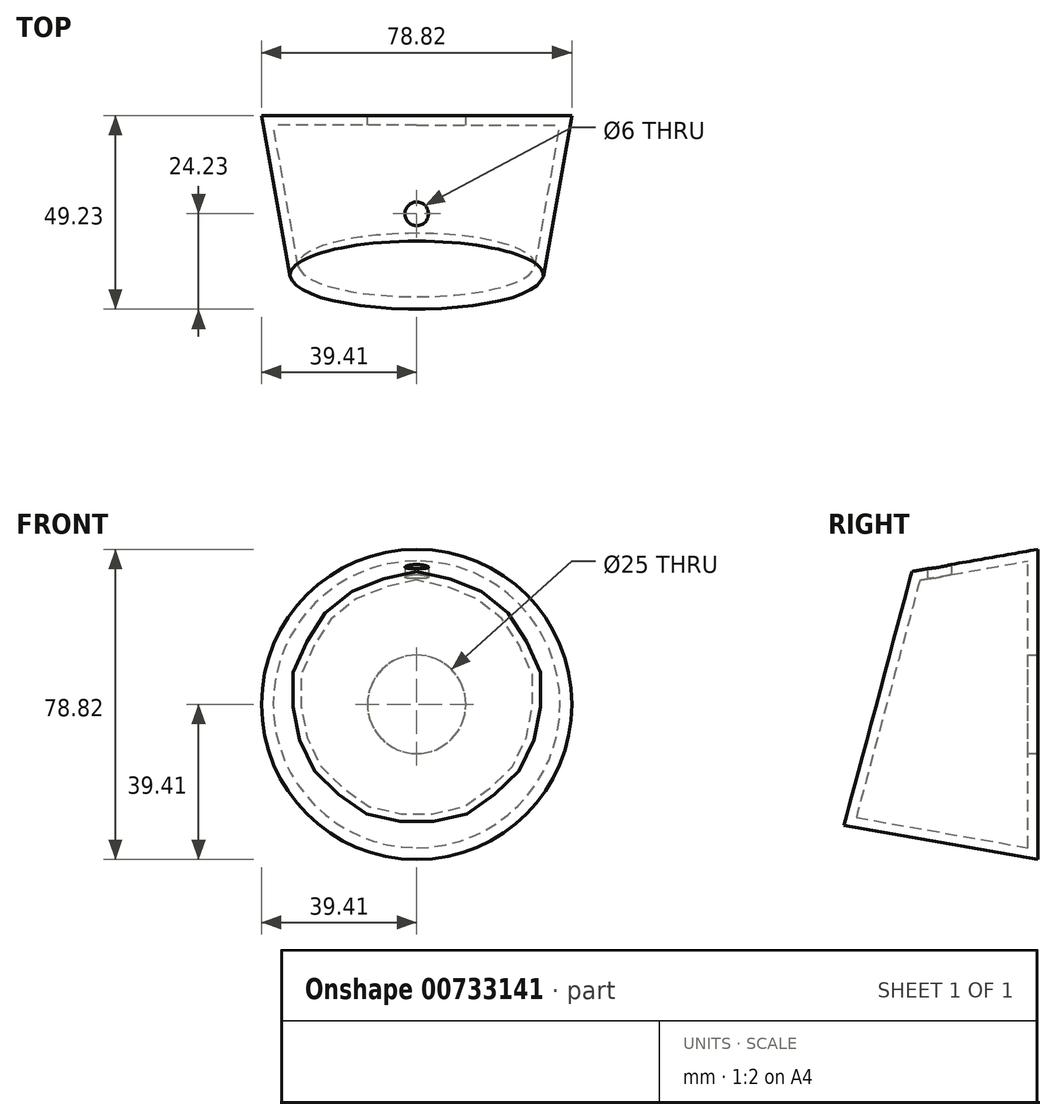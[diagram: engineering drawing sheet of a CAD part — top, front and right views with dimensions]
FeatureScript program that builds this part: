
annotation { "Feature Type Name" : "Feature", "Feature Type Description" : "" }
export const myFeature = defineFeature(function(context is Context, id is Id, definition is map)
    precondition{}
    {
        {
            var Q0;
            Q0=qCreatedBy(makeId("Front.planeOp"),FACE);
            var sketch = newSketch(context, id + "F0", { "sketchPlane" : qUnion([Q0])});
            skCircle(sketch, "E0", {"center": v(0, 0) * mm, "radius": 35 * mm});
            skSolve(sketch);
        }
        {
            var Q0;
            Q0=makeQuery(id+"F0.imprint","IMPRINT",FACE,{"disambiguationData":[TD([[makeQuery(id+"F0.imprint","IMPRINT",EDGE,{"derivedFrom":sQuery(id+"F0.wireOp",EDGE,"E0")}),1.0]])]});
            var Q1;
            Q1=sQuery(id+"F0.wireOp",EDGE,"E0");
            extrude(context, id + "F1", {"entities" : qUnion([Q0]), "surfaceEntities" : qUnion([Q1]), "oppositeDirection" : true, "depth" : 25 * mm, "offsetDistance" : 25 * mm, "hasDraft" : true, "draftAngle" : 10 * degree});
        }
        {
            var Q0;
            Q0 = qSketchRegion(id + "F0", true);
            extrude(context, id + "F2", {"entities" : qUnion([Q0]), "operationType" : NewBodyOperationType.ADD, "depth" : 25 * mm, "offsetDistance" : 25 * mm, "hasDraft" : true, "draftAngle" : 10 * degree, "draftPullDirection" : true});
        }
        {
            var Q0;
            Q0=qCreatedBy(makeId("Right.planeOp"),FACE);
            var sketch = newSketch(context, id + "F3", { "sketchPlane" : qUnion([Q0])});
            skLineSegment(sketch, "E1", {"start": v(-5.75, 38.26) * mm, "end": v(-29.22, -49.32) * mm});
            skLineSegment(sketch, "E2", {"start": v(-5.75, 38.26) * mm, "end": v(-37.5, 38.26) * mm});
            skLineSegment(sketch, "E3", {"start": v(-37.5, 38.26) * mm, "end": v(-37.5, -49.69) * mm});
            skLineSegment(sketch, "E4", {"start": v(-29.22, -49.32) * mm, "end": v(-37.5, -49.69) * mm});
            skLineSegment(sketch, "E5", {"start": v(-99.85, 0) * mm, "end": v(0, 0) * mm, "construction": true});
            skSolve(sketch);
        }
        {
            var Q0;
            Q0=makeQuery(id+"F3.imprint","IMPRINT",FACE,{"disambiguationData":[TD([[makeQuery(id+"F3.imprint","IMPRINT",EDGE,{"derivedFrom":sQuery(id+"F3.wireOp",EDGE,"E1")}),-1.0]])]});
            extrude(context, id + "F4", {"entities" : qUnion([Q0]), "operationType" : NewBodyOperationType.REMOVE, "endBound" : BoundingType.SYMMETRIC, "oppositeDirection" : true, "depth" : 80 * mm, "offsetDistance" : 25 * mm});
        }
        {
            var Q0;
            Q0=makeQuery(id+"F1.opExtrude","CAP_FACE",FACE,{"disambiguationData":[OSD([sQuery(id+"F0.wireOp",EDGE,"E0")])],"isStart":true});
            var Q1;
            Q1=makeQuery(id+"F1.*.split.splitOp","SPLIT",FACE,{"derivedFrom":makeQuery(id+"F1.opExtrude","SWEPT_FACE",FACE,{"disambiguationData":[OSD([sQuery(id+"F0.wireOp",EDGE,"E0")])]}),"isFromBackBody":true});
            var Q2;
            Q2=makeQuery(id+"F1.*.split.splitOp","SPLIT",FACE,{"derivedFrom":makeQuery(id+"F1.opExtrude","SWEPT_FACE",FACE,{"disambiguationData":[OSD([sQuery(id+"F0.wireOp",EDGE,"E0")])]})});
            var Q3;
            Q3=makeQuery(id+"F4.boolean.opBoolean","COPY",FACE,{"derivedFrom":makeQuery(id+"F4.opExtrude","SWEPT_FACE",FACE,{"disambiguationData":[OSD([sQuery(id+"F3.wireOp",EDGE,"E1")])]})});
            var Q4;
            Q4=makeQuery(id+"F1.*.split.splitOp","SPLIT",BODY,{"derivedFrom":makeQuery(id+"F1.opExtrude","SWEPT_BODY",BODY,{"disambiguationData":[OSD([sQuery(id+"F0.wireOp",EDGE,"E0")])]})});
            shell(context, id + "F5", {"isHollow" : true, "entities" : qUnion([Q0, Q1, Q2, Q3]), "parts" : qUnion([Q4]), "thickness" : 2.5 * mm});
        }
        {
            var Q0;
            Q0=qCreatedBy(makeId("Top.planeOp"),FACE);
            var sketch = newSketch(context, id + "F6", { "sketchPlane" : qUnion([Q0])});
            skPoint(sketch, "E6", {"position": v(0, 0) * mm});
            skSolve(sketch);
        }
        {
            var Q0;
            Q0=sQuery(id+"F6.wireOp",VERTEX,"E6");
            var Q1;
            Q1=makeQuery(id+"F1.*.split.splitOp","SPLIT",BODY,{"derivedFrom":makeQuery(id+"F1.opExtrude","SWEPT_BODY",BODY,{"disambiguationData":[OSD([sQuery(id+"F0.wireOp",EDGE,"E0")])]})});
            hole(context, id + "F7", {"style" : HoleStyle.SIMPLE, "endStyle" : HoleEndStyle.THROUGH, "oppositeDirection" : true, "holeDiameter" : 6 * mm, "majorDiameter" : 5 * mm, "isTappedThrough" : true, "tappedDepth" : 12 * mm, "tapClearance" : 3, "locations" : qUnion([Q0]), "scope" : qUnion([Q1])});
        }
        {
            var Q0;
            Q0=makeQuery(id+"F1.opExtrude","CAP_FACE",FACE,{"disambiguationData":[OSD([sQuery(id+"F0.wireOp",EDGE,"E0")])],"isStart":false});
            var sketch = newSketch(context, id + "F8", { "sketchPlane" : qUnion([Q0])});
            skCircle(sketch, "E7", {"center": v(0, 0) * mm, "radius": 12.5 * mm});
            skSolve(sketch);
        }
        {
            var Q0;
            Q0=makeQuery(id+"F8.imprint","IMPRINT",FACE,{"disambiguationData":[TD([[makeQuery(id+"F8.imprint","IMPRINT",EDGE,{"derivedFrom":sQuery(id+"F8.wireOp",EDGE,"E7")}),1.0]])]});
            extrude(context, id + "F9", {"entities" : qUnion([Q0]), "operationType" : NewBodyOperationType.REMOVE, "endBound" : BoundingType.UP_TO_NEXT, "oppositeDirection" : true, "depth" : 25 * mm, "offsetDistance" : 25 * mm});
        }
    });
